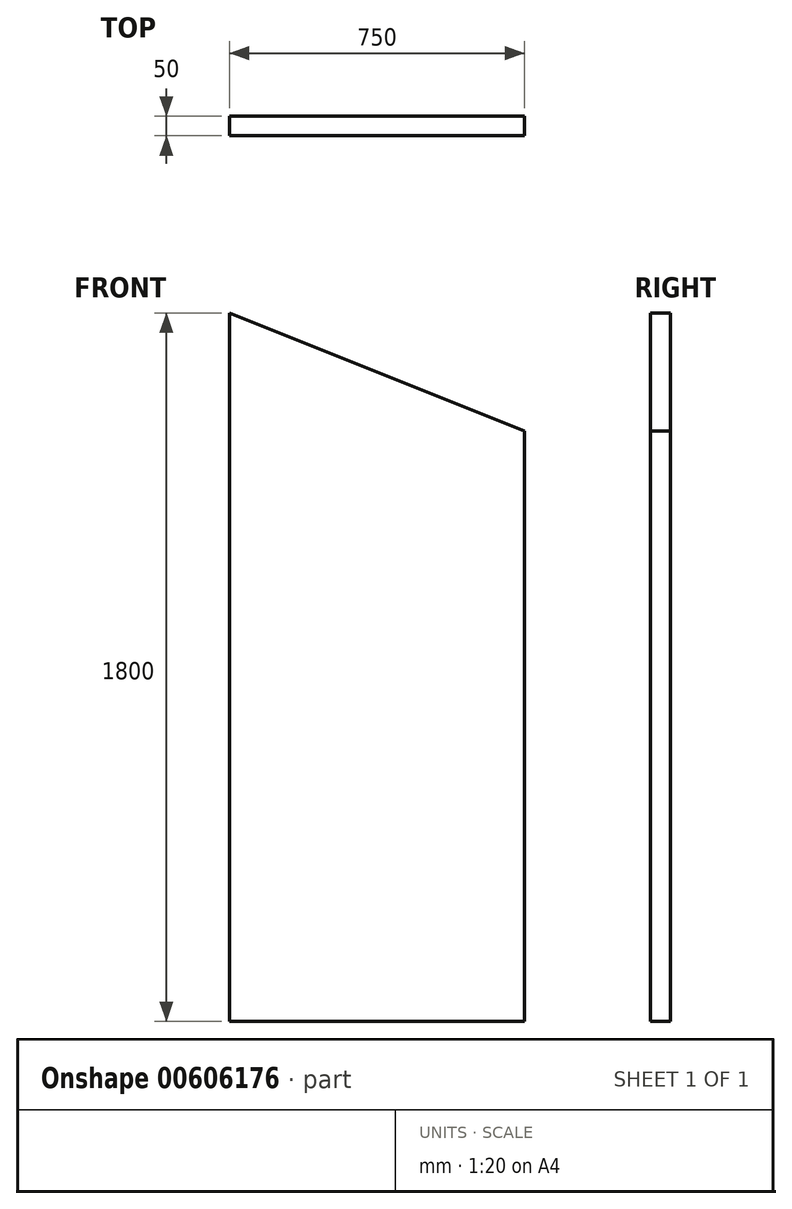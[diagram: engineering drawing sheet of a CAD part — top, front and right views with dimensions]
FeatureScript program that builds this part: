
annotation { "Feature Type Name" : "Feature", "Feature Type Description" : "" }
export const myFeature = defineFeature(function(context is Context, id is Id, definition is map)
    precondition{}
    {
        {
            var Q0;
            Q0=qCreatedBy(makeId("Front.planeOp"),FACE);
            var sketch = newSketch(context, id + "F0", { "sketchPlane" : qUnion([Q0])});
            skLineSegment(sketch, "E0.top", {"start": v(375, -900) * mm, "end": v(-375, -900) * mm});
            skLineSegment(sketch, "E0.right", {"start": v(-375, 900) * mm, "end": v(-375, -900) * mm});
            skPoint(sketch, "E0.middle", {"position": v(0, 0) * mm});
            skLineSegment(sketch, "E1", {"start": v(-375, 900) * mm, "end": v(375, 600) * mm});
            skLineSegment(sketch, "E2", {"start": v(375, 600) * mm, "end": v(375, -900) * mm});
            skSolve(sketch);
        }
        {
            var Q0;
            Q0=qSketchRegion(id+"F0",true);
            extrude(context, id + "F1", {"entities" : qUnion([Q0]), "depth" : 50 * mm, "offsetDistance" : 25.4 * mm});
        }
    });
